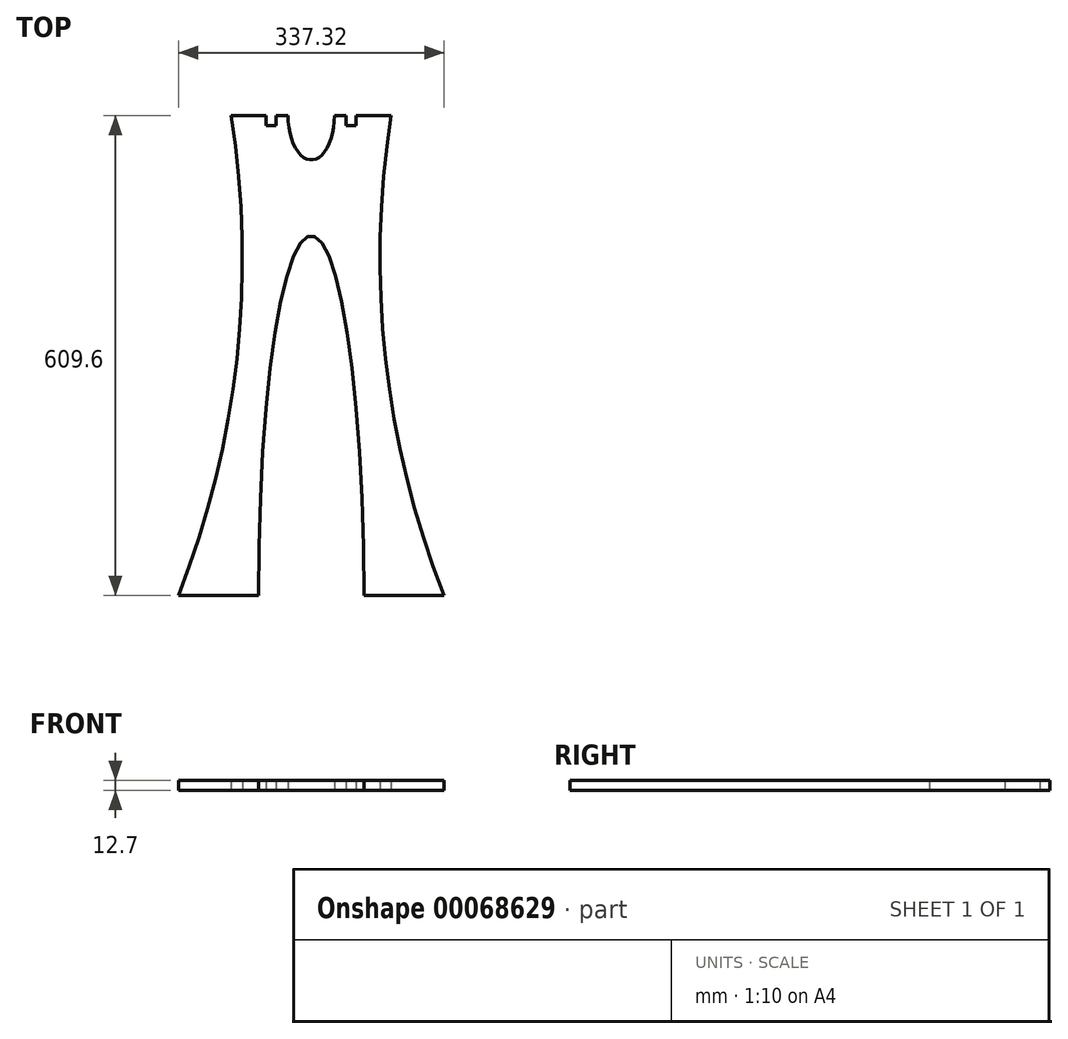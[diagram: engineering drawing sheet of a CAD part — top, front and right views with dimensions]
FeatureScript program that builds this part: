
annotation { "Feature Type Name" : "Feature", "Feature Type Description" : "" }
export const myFeature = defineFeature(function(context is Context, id is Id, definition is map)
    precondition{}
    {
        {
            var Q0;
            Q0=qCreatedBy(makeId("Top.planeOp"),FACE);
            var sketch = newSketch(context, id + "F0", { "sketchPlane" : qUnion([Q0])});
            skLineSegment(sketch, "E0", {"start": v(67.06, 0) * mm, "end": v(168.66, 0) * mm});
            skEllipticalArc(sketch, "E1", {});
            skLineSegment(sketch, "E2", {"start": v(0, 0) * mm, "end": v(0, 123.76) * mm, "construction": true});
            skLineSegment(sketch, "E3", {"start": v(101.6, 609.6) * mm, "end": v(57.15, 609.6) * mm});
            skArc(sketch, "E4", {"start": v(101.6, 609.6) * mm, "mid": v(94.42, 300.32) * mm, "end": v(168.66, 0) * mm});
            skLineSegment(sketch, "E5.top", {"start": v(44.45, 596.9) * mm, "end": v(57.15, 596.9) * mm});
            skLineSegment(sketch, "E5.left", {"start": v(44.45, 609.6) * mm, "end": v(44.45, 596.9) * mm});
            skLineSegment(sketch, "E5.right", {"start": v(57.15, 609.6) * mm, "end": v(57.15, 596.9) * mm});
            skLineSegment(sketch, "E6.trimOffspring", {"start": v(44.45, 609.6) * mm, "end": v(29.43, 609.6) * mm});
            skLineSegment(sketch, "E7.MirrorCS", {"start": v(-44.45, 609.6) * mm, "end": v(-44.45, 596.9) * mm});
            skLineSegment(sketch, "E8.MirrorCS", {"start": v(-44.45, 596.9) * mm, "end": v(-57.15, 596.9) * mm});
            skLineSegment(sketch, "E9.MirrorCS", {"start": v(-57.15, 609.6) * mm, "end": v(-57.15, 596.9) * mm});
            skLineSegment(sketch, "E10.MirrorCS", {"start": v(-101.6, 609.6) * mm, "end": v(-57.15, 609.6) * mm});
            skArc(sketch, "E11.MirrorCS", {"start": v(-101.6, 609.6) * mm, "mid": v(-94.42, 300.32) * mm, "end": v(-168.66, 0) * mm});
            skEllipticalArc(sketch, "E12.MirrorCS", {});
            skLineSegment(sketch, "E13.MirrorCS", {"start": v(-44.45, 609.6) * mm, "end": v(-29.43, 609.6) * mm});
            skLineSegment(sketch, "E14.MirrorCS", {"start": v(-67.06, 0) * mm, "end": v(-168.66, 0) * mm});
            skEllipticalArc(sketch, "E15", {});
            const initialGuessF0  = {"E1": [0, 0, 0, 1, 0.4572, 0.0670599073778803, 4.71238898038469, 0], "E12.MirrorCS": [0, 0, 0, 1, 0.4572, 0.0670599073778803, 0, 1.5707963267948966], "E15": [0, 0.6096, 0, -1, 0.056401483631134064, 0.029432116035537106, 4.71238898038469, 1.5707963267948966]};
            skSetInitialGuess(sketch, initialGuessF0);
            skSolve(sketch);
        }
        {
            var Q0;
            Q0 = qSketchRegion(id + "F0", true);
            extrude(context, id + "F1", {"entities" : qUnion([Q0]), "depth" : 12.7 * mm});
        }
    });
